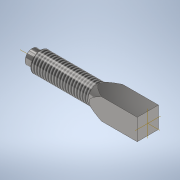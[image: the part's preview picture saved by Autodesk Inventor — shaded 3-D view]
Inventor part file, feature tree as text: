
AUTODESK INVENTOR PART (.ipt)
format: ipt  version: 2021.1 (Build 251245000, 245)  size: 133,120 bytes
history: native  units: in
note: dims shown in document units (in); Inventor stores cm internally (conversion verified against a paired STEP export)
features: sketch x2, revolve x1, thread x1, extrude x1
ambient origin geometry x8: Origin, YZ Plane, XZ Plane, XY Plane, X Axis, Y Axis, Z Axis, Center Point
bodies: Solid1 (feature_tree)
feature tree (5):
  revolve  "Revolution1"  [1 undecoded]
  thread  "Thread1"  [1 undecoded]
  extrude  "Extrusion1"  Depth=0.4134in
  sketch  "Sketch1"  dims[d7=0.1969in d8=0.2362in d9=0.2756in]
  sketch  "Sketch2"  dims[d10=0.9843in d11=1.9685in d12=0.3937in d13=0.4134in d14=90.0deg d15=1.5748in d16=0.0in d17=0.3937in d18=0.0in]
note: 2 required parameter values undecoded (feature->parameter linkage not recoverable at this tier; creation-order binding heuristic only, values carry confidence <= 0.55)